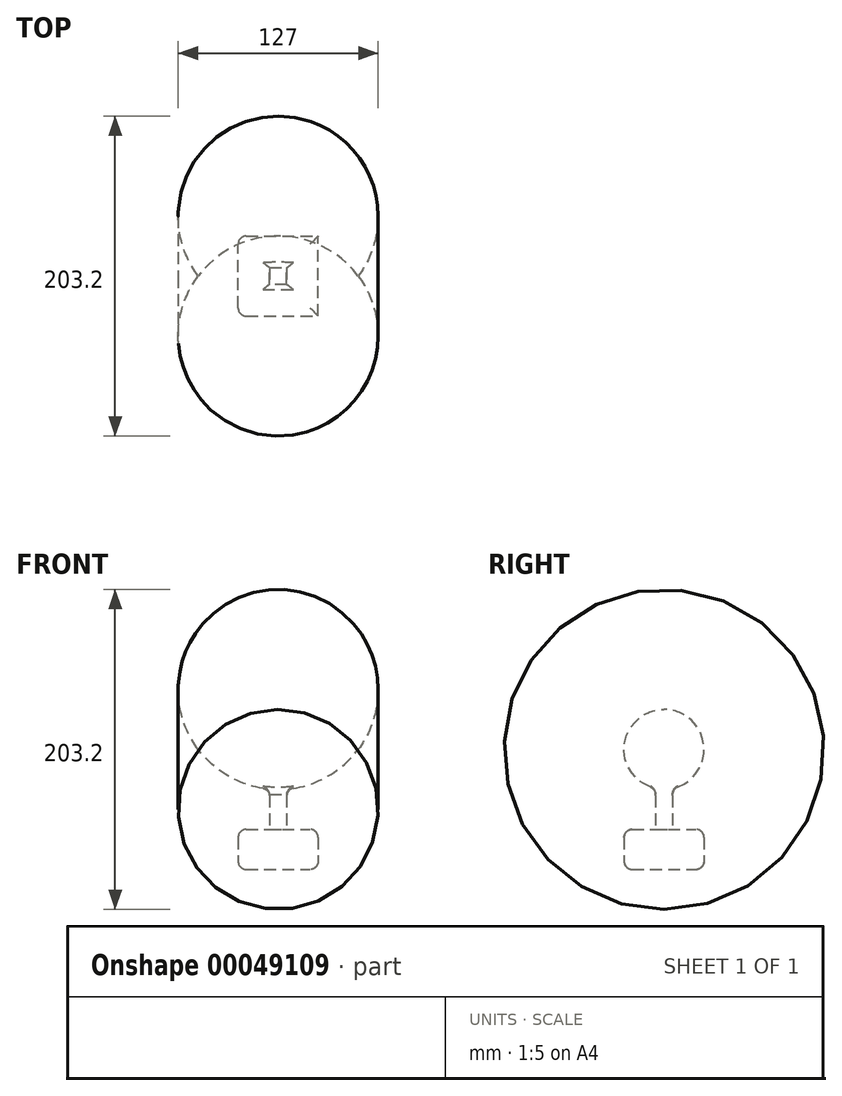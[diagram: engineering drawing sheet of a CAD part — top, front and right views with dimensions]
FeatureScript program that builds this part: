
annotation { "Feature Type Name" : "Feature", "Feature Type Description" : "" }
export const myFeature = defineFeature(function(context is Context, id is Id, definition is map)
    precondition{}
    {
        {
            var Q0;
            Q0=qCreatedBy(makeId("Top.planeOp"),FACE);
            var sketch = newSketch(context, id + "F0", { "sketchPlane" : qUnion([Q0])});
            skLineSegment(sketch, "E0.bottom", {"start": v(0, 0) * mm, "end": v(50.8, 0) * mm});
            skLineSegment(sketch, "E0.top", {"start": v(0, 50.8) * mm, "end": v(50.8, 50.8) * mm});
            skLineSegment(sketch, "E0.left", {"start": v(0, 0) * mm, "end": v(0, 50.8) * mm});
            skLineSegment(sketch, "E0.right", {"start": v(50.8, 0) * mm, "end": v(50.8, 50.8) * mm});
            skSolve(sketch);
        }
        {
            var Q0;
            Q0 = qSketchRegion(id + "F0", true);
            extrude(context, id + "F1", {"entities" : qUnion([Q0]), "depth" : 25.4 * mm});
        }
        {
            var Q0;
            Q0=makeQuery(id+"F1.opExtrude","CAP_FACE",FACE,{"disambiguationData":[OSD([sQuery(id+"F0.wireOp",EDGE,"E0.bottom"),sQuery(id+"F0.wireOp",EDGE,"E0.top"),sQuery(id+"F0.wireOp",EDGE,"E0.left"),sQuery(id+"F0.wireOp",EDGE,"E0.right")])],"isStart":false});
            var sketch = newSketch(context, id + "F2", { "sketchPlane" : qUnion([Q0])});
            skLineSegment(sketch, "E1", {"start": v(25.4, 30.8) * mm, "end": v(30.8, 30.8) * mm});
            skLineSegment(sketch, "E2", {"start": v(30.8, 30.8) * mm, "end": v(30.8, 20) * mm});
            skLineSegment(sketch, "E3", {"start": v(30.8, 20) * mm, "end": v(20, 20) * mm});
            skLineSegment(sketch, "E4", {"start": v(20, 20) * mm, "end": v(20, 30.8) * mm});
            skLineSegment(sketch, "E5", {"start": v(20, 30.8) * mm, "end": v(25.4, 30.8) * mm});
            skSolve(sketch);
        }
        {
            var Q0;
            Q0 = qSketchRegion(id + "F2", true);
            extrude(context, id + "F3", {"entities" : qUnion([Q0]), "operationType" : NewBodyOperationType.ADD, "depth" : 50.8 * mm});
        }
        {
            var Q0;
            Q0=makeQuery(id+"F3.opExtrude","CAP_FACE",FACE,{"disambiguationData":[OSD([sQuery(id+"F2.wireOp",EDGE,"E1"),sQuery(id+"F2.wireOp",EDGE,"E2"),sQuery(id+"F2.wireOp",EDGE,"E3"),sQuery(id+"F2.wireOp",EDGE,"E4"),sQuery(id+"F2.wireOp",EDGE,"E5")])],"isStart":false});
            var sketch = newSketch(context, id + "F4", { "sketchPlane" : qUnion([Q0])});
            skArc(sketch, "E6", {"start": v(76.2, 25.4) * mm, "mid": v(53.8, 44.1) * mm, "end": v(25.4, 50.8) * mm});
            skArc(sketch, "E7.MirrorCS", {"start": v(-25.4, 25.4) * mm, "mid": v(-3, 44.1) * mm, "end": v(25.4, 50.8) * mm});
            skArc(sketch, "E8.MirrorCS", {"start": v(-25.4, 25.4) * mm, "mid": v(-3, 6.7) * mm, "end": v(25.4, 0) * mm});
            skArc(sketch, "E9.MirrorCS", {"start": v(76.2, 25.4) * mm, "mid": v(53.8, 6.7) * mm, "end": v(25.4, 0) * mm});
            skLineSegment(sketch, "E10", {"start": v(-25.4, 25.4) * mm, "end": v(76.2, 25.4) * mm});
            skSolve(sketch);
        }
        {
            var Q0;
            {var subQ6=sQuery(id+"F4.wireOp",EDGE,"E6");Q0=makeQuery(id+"F4.imprint","IMPRINT",FACE,{"disambiguationData":[TD([[makeQuery(id+"F4.imprint","IMPRINT",EDGE,{"derivedFrom":subQ6}),1.0]])]});}
            var Q1;
            {var subQ3=makeQuery(id+"F3.opExtrude","CAP_EDGE",EDGE,{"disambiguationData":[OSD([sQuery(id+"F2.wireOp",EDGE,"E1"),sQuery(id+"F2.wireOp",EDGE,"E5")])],"isStart":false});Q1=makeQuery(id+"F4.imprint","IMPRINT",FACE,{"disambiguationData":[TD([[makeQuery(id+"F4.imprint","IMPRINT",EDGE,{"derivedFrom":subQ3}),-1.0]])]});}
            var Q2;
            Q2=sQuery(id+"F4.wireOp",EDGE,"E10");
            revolve(context, id + "F5", {"operationType" : NewBodyOperationType.ADD, "entities" : qUnion([Q0, Q1]), "axis" : qUnion([Q2]), "revolveType" : RevolveType.FULL});
        }
        {
            var Q0;
            Q0=makeQuery(id+"F1.opExtrude","CAP_EDGE",EDGE,{"disambiguationData":[OSD([sQuery(id+"F0.wireOp",EDGE,"E0.right")])],"isStart":false});
            var Q1;
            Q1=makeQuery(id+"F1.opExtrude","CAP_EDGE",EDGE,{"disambiguationData":[OSD([sQuery(id+"F0.wireOp",EDGE,"E0.top")])],"isStart":false});
            var Q2;
            Q2=makeQuery(id+"F1.opExtrude","CAP_EDGE",EDGE,{"disambiguationData":[OSD([sQuery(id+"F0.wireOp",EDGE,"E0.left")])],"isStart":false});
            var Q3;
            Q3=makeQuery(id+"F1.opExtrude","CAP_EDGE",EDGE,{"disambiguationData":[OSD([sQuery(id+"F0.wireOp",EDGE,"E0.bottom")])],"isStart":false});
            var Q4;
            Q4=makeQuery(id+"F1.opExtrude","CAP_EDGE",EDGE,{"disambiguationData":[OSD([sQuery(id+"F0.wireOp",EDGE,"E0.bottom")])],"isStart":true});
            var Q5;
            Q5=makeQuery(id+"F1.opExtrude","CAP_EDGE",EDGE,{"disambiguationData":[OSD([sQuery(id+"F0.wireOp",EDGE,"E0.right")])],"isStart":true});
            var Q6;
            Q6=makeQuery(id+"F1.opExtrude","CAP_EDGE",EDGE,{"disambiguationData":[OSD([sQuery(id+"F0.wireOp",EDGE,"E0.top")])],"isStart":true});
            var Q7;
            Q7=makeQuery(id+"F1.opExtrude","CAP_EDGE",EDGE,{"disambiguationData":[OSD([sQuery(id+"F0.wireOp",EDGE,"E0.left")])],"isStart":true});
            var Q8;
            Q8=makeQuery(id+"F3.opExtrude","CAP_EDGE",EDGE,{"disambiguationData":[OSD([sQuery(id+"F2.wireOp",EDGE,"E4")])],"isStart":true});
            var Q9;
            Q9=makeQuery(id+"F3.opExtrude","CAP_EDGE",EDGE,{"disambiguationData":[OSD([sQuery(id+"F2.wireOp",EDGE,"E3")])],"isStart":true});
            var Q10;
            Q10=makeQuery(id+"F3.opExtrude","CAP_EDGE",EDGE,{"disambiguationData":[OSD([sQuery(id+"F2.wireOp",EDGE,"E1"),sQuery(id+"F2.wireOp",EDGE,"E5")])],"isStart":true});
            var Q11;
            Q11=makeQuery(id+"F3.opExtrude","CAP_EDGE",EDGE,{"disambiguationData":[OSD([sQuery(id+"F2.wireOp",EDGE,"E2")])],"isStart":true});
            var Q12;
            Q12=makeQuery(id+"F5.boolean.opBoolean","INTERSECT",EDGE,{"derivedFrom":[makeQuery(id+"F3.opExtrude","SWEPT_FACE",FACE,{"disambiguationData":[OSD([sQuery(id+"F2.wireOp",EDGE,"E2")])]}),makeQuery(id+"F5.opRevolve","SWEPT_FACE",FACE,{"disambiguationData":[OSD([sQuery(id+"F4.wireOp",EDGE,"E6"),sQuery(id+"F4.wireOp",EDGE,"E7.MirrorCS")])]})]});
            var Q13;
            Q13=makeQuery(id+"F5.boolean.opBoolean","INTERSECT",EDGE,{"derivedFrom":[makeQuery(id+"F3.opExtrude","SWEPT_FACE",FACE,{"disambiguationData":[OSD([sQuery(id+"F2.wireOp",EDGE,"E3")])]}),makeQuery(id+"F5.opRevolve","SWEPT_FACE",FACE,{"disambiguationData":[OSD([sQuery(id+"F4.wireOp",EDGE,"E6"),sQuery(id+"F4.wireOp",EDGE,"E7.MirrorCS")])]})]});
            var Q14;
            Q14=makeQuery(id+"F5.boolean.opBoolean","INTERSECT",EDGE,{"derivedFrom":[makeQuery(id+"F3.opExtrude","SWEPT_FACE",FACE,{"disambiguationData":[OSD([sQuery(id+"F2.wireOp",EDGE,"E1"),sQuery(id+"F2.wireOp",EDGE,"E5")])]}),makeQuery(id+"F5.opRevolve","SWEPT_FACE",FACE,{"disambiguationData":[OSD([sQuery(id+"F4.wireOp",EDGE,"E6"),sQuery(id+"F4.wireOp",EDGE,"E7.MirrorCS")])]})]});
            var Q15;
            Q15=makeQuery(id+"F5.boolean.opBoolean","INTERSECT",EDGE,{"derivedFrom":[makeQuery(id+"F3.opExtrude","SWEPT_FACE",FACE,{"disambiguationData":[OSD([sQuery(id+"F2.wireOp",EDGE,"E4")])]}),makeQuery(id+"F5.opRevolve","SWEPT_FACE",FACE,{"disambiguationData":[OSD([sQuery(id+"F4.wireOp",EDGE,"E6"),sQuery(id+"F4.wireOp",EDGE,"E7.MirrorCS")])]})]});
            var Q16;
            Q16=makeQuery(id+"F1.opExtrude","SWEPT_FACE",FACE,{"disambiguationData":[OSD([sQuery(id+"F0.wireOp",EDGE,"E0.left")])]});
            fillet(context, id + "F6", {"entities" : qUnion([Q0, Q1, Q2, Q3, Q4, Q5, Q6, Q7, Q8, Q9, Q10, Q11, Q12, Q13, Q14, Q15, Q16]), "radius" : 5.08 * mm, "tangentPropagation" : true, "allowEdgeOverflow" : false});
        }
    });
